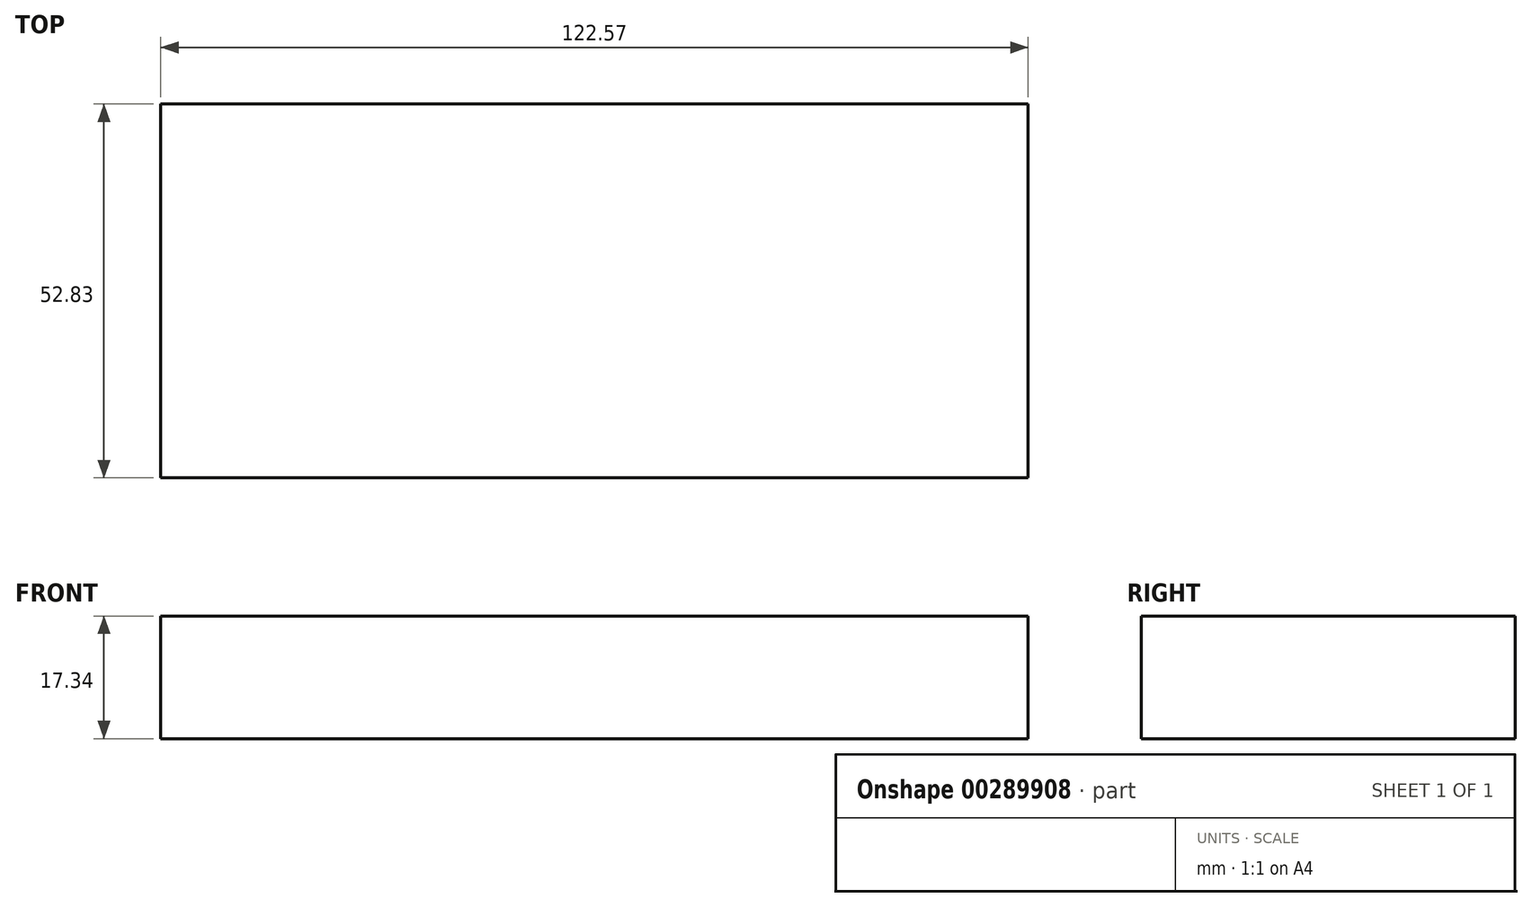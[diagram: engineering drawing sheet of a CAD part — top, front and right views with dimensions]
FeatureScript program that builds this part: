
annotation { "Feature Type Name" : "Feature", "Feature Type Description" : "" }
export const myFeature = defineFeature(function(context is Context, id is Id, definition is map)
    precondition{}
    {
        {
            var Q0;
            Q0=qCreatedBy(makeId("Front.planeOp"),FACE);
            var sketch = newSketch(context, id + "F0", { "sketchPlane" : qUnion([Q0])});
            skSolve(sketch);
        }
        {
            var Q0;
            Q0=qCreatedBy(makeId("Front.planeOp"),FACE);
            var sketch = newSketch(context, id + "F1", { "sketchPlane" : qUnion([Q0])});
            skLineSegment(sketch, "E0.bottom", {"start": v(-59.57, 0) * mm, "end": v(-182.14, 0) * mm});
            skLineSegment(sketch, "E0.top", {"start": v(-59.57, -17.34) * mm, "end": v(-182.14, -17.34) * mm});
            skLineSegment(sketch, "E0.left", {"start": v(-59.57, -17.34) * mm, "end": v(-59.57, 0) * mm});
            skLineSegment(sketch, "E0.right", {"start": v(-182.14, -17.34) * mm, "end": v(-182.14, 0) * mm});
            skPoint(sketch, "E0.middle", {"position": v(-120.86, -8.67) * mm});
            skSolve(sketch);
        }
        {
            var Q0;
            Q0=sQuery(id+"F1.wireOp",EDGE,"E0.right");
            var Q1;
            Q1=sQuery(id+"F1.wireOp",EDGE,"E0.top");
            var Q2;
            Q2=sQuery(id+"F1.wireOp",EDGE,"E0.bottom");
            var Q3;
            Q3=sQuery(id+"F1.wireOp",EDGE,"E0.left");
            var Q4;
            Q4 = qConstructionFilter(qBodyType(qCreatedBy(id + "F0" ,EDGE), BodyType.WIRE), ConstructionObject.NO);
            extrude(context, id + "F2", {"bodyType" : ToolBodyType.SURFACE, "surfaceEntities" : qUnion([Q0, Q1, Q2, Q3, Q4]), "depth" : 52.83 * mm});
        }
    });
